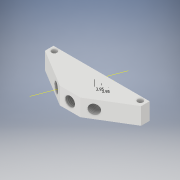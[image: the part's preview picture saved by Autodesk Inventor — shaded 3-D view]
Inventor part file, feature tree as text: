
AUTODESK INVENTOR PART (.ipt)
format: ipt  version: 2018 (Build 220112000, 112)  size: 184,832 bytes
history: native  units: in
note: dims shown in document units (in); Inventor stores cm internally (conversion verified against a paired STEP export)
features: sketch x13, extrude x7, other x6, thread x5, hole x2
ambient origin geometry x8: Origin, YZ Plane, XZ Plane, XY Plane, X Axis, Y Axis, Z Axis, Center Point
bodies: Solid1 (feature_tree)
feature tree (33):
  extrude  "Extrusion1"  Depth=1.1122in
  extrude  "Extrusion2"  Depth=0.7283in
  extrude  "Extrusion3"  Depth=0.1969in
  thread  "Thread1"  [1 undecoded]
  extrude  "Extrusion4"  Depth=0.1181in
  extrude  "Extrusion5"  Depth=0.3937in
  thread  "Thread2"  [1 undecoded]
  thread  "Thread3"  [1 undecoded]
  extrude  "Extrusion6"  Depth=0.1969in
  sketch  "Sketch14"  dims[d17=0.2756in d18=0.0in d19=0.3937in d20=0.0in]
  other  "Work Point2"
  sketch  "Sketch19"  dims[d21=0.2268in d22=0.2362in]
  other  "Work Point5"
  sketch  "3D Sketch5"
  other  "Work Axis3"
  hole  "Hole1"  [1 undecoded]
  sketch  "Sketch20"  dims[d23=0.1969in d24=0.2756in d25=0.0in d26=0.2268in d27=0.1969in]
  other  "Work Point6"
  sketch  "Sketch21"  dims[d28=0.2362in]
  other  "Work Point7"
  sketch  "3D Sketch6"
  other  "Work Axis4"
  hole  "Hole2"  [1 undecoded]
  extrude  "Extrusion7"  Depth=0.2756in TaperAngle=0.0deg
  thread  "Thread4"  [1 undecoded]
  thread  "Thread5"  [1 undecoded]
  sketch  "Sketch1"  dims[d0=1.1122in d1=1.1122in]
  sketch  "Sketch2"  dims[d2=0.7283in d3=0.2362in]
  sketch  "Sketch3"  dims[d4=0.2362in d5=0.1969in d6=0.3937in d7=0.0in]
  sketch  "Sketch4"  dims[d8=0.126in d9=0.1181in]
  sketch  "Sketch5"  dims[d10=0.0984in d11=0.126in d12=0.1181in d13=0.3937in d14=0.0in]
  sketch  "Sketch6"  dims[d15=0.2268in d16=0.1969in]
  sketch  "Sketch23"  dims[d29=0.2756in d30=0.0in d31=0.3937in d32=0.0in d33=0.3937in d34=0.0in d35=0.0591in d36=0.4724in d37=0.0in d50=0.1555in d60=0.3937in d61=0.3937in d53=0.07in d54=0.2362in d55=0.1575in d56=0.0787in d57=90.0deg d58=0.7973in d59=0.7559in d62=0.1555in d63=0.3937in d64=0.3937in d65=0.0591in d66=0.2362in d67=0.1575in d68=0.0787in d69=90.0deg d70=0.7973in d71=0.7559in d72=0.0984in d73=0.6693in d74=0.0984in d75=0.4921in d76=0.1969in d77=0.0in d78=0.3937in d79=0.0in d80=0.3937in d81=0.0in d44=0.0394in d45=0.0394in d47=0.0394in d48=0.0394in d51=0.0394in d52=0.0394in]
note: 7 required parameter values undecoded (feature->parameter linkage not recoverable at this tier; creation-order binding heuristic only, values carry confidence <= 0.55)
